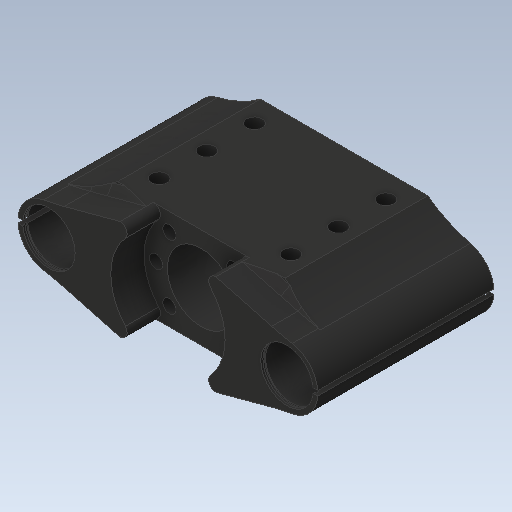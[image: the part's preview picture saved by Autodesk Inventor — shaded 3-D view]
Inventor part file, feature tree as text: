
AUTODESK INVENTOR PART (.ipt)
format: ipt  version: 2020 (Build 240168000, 168)  size: 548,352 bytes
history: native  units: mm
features: sketch x24, extrude x17, other x10, mirror x6, chamfer x5, fillet x3, pattern_circular x2, pattern_linear x1
ambient origin geometry x8: Origin, YZ Plane, XZ Plane, XY Plane, X Axis, Y Axis, Z Axis, Center Point
bodies: Body1 (feature_tree)
feature tree (68):
  other  "Bryła1"
  other  "Opisy"
  extrude  "Wyciągnięcie proste1"  Depth=22.0mm
  extrude  "Wyciągnięcie proste2"  Depth=26.0mm
  other  "Płaszczyzna konstrukcyjna1"
  extrude  "Wyciągnięcie proste3"  Depth=74.0mm TaperAngle=0.0deg
  extrude  "Wyciągnięcie proste4"  Depth=2.0mm
  other  "Płaszczyzna konstrukcyjna2"
  extrude  "Wyciągnięcie proste5"  Depth=1.0mm
  other  "Płaszczyzna konstrukcyjna3"
  mirror  "Odbij1"
  extrude  "Wyciągnięcie proste6"  Depth=80.0mm TaperAngle=0.0deg
  other  "Płaszczyzna konstrukcyjna4"
  mirror  "Odbij2"
  extrude  "Wyciągnięcie proste7"  [1 undecoded]
  sketch  "Szkic9"
  extrude  "Wyciągnięcie proste8"  Depth=22.0mm
  extrude  "Wyciągnięcie proste9"  Depth=19.0mm
  fillet  "Zaokrąglenie1"  Radius=6.0mm
  extrude  "Wyciągnięcie proste10"  Depth=2.0mm
  mirror  "Odbij3"
  chamfer  "Faza1"  Distance=6.0mm
  other  "Płaszczyzna konstrukcyjna5"
  chamfer  "Faza2"  [1 undecoded]
  chamfer  "Faza3"  Distance=23.0mm
  chamfer  "Faza4"  Distance=1.1mm
  fillet  "Zaokrąglenie2"  [1 undecoded]
  sketch  "Szkic13"
  extrude  "Wyciągnięcie proste13"  Depth=8.0mm
  extrude  "Wyciągnięcie proste14"  Depth=100.0mm
  pattern_circular  "Szyk kołowy3"  [2 undecoded]
  pattern_circular  "Szyk kołowy4"  Count=10  [1 undecoded]
  mirror  "Odbij5"
  extrude  "Wyciągnięcie proste15"  Depth=8.0mm
  extrude  "Wyciągnięcie proste16"  Depth=74.0mm TaperAngle=0.0deg
  extrude  "Wyciągnięcie proste17"  [1 undecoded]
  mirror  "Odbij6"
  fillet  "Zaokrąglenie3"  Radius=2.0mm
  chamfer  "Faza5"  Distance=74.0mm
  other  "Płaszczyzna konstrukcyjna6"
  sketch  "Szkic21"
  sketch  "Szkic22"
  extrude  "Wyciągnięcie proste18"  Depth=48.0mm
  pattern_linear  "Szyk prostokątny1"  Count1=5  [1 undecoded]
  mirror  "Odbij7"
  sketch  "Szkic24"
  sketch  "Szkic25"
  extrude  "Wyciągnięcie proste19"  Depth=14.0mm TaperAngle=0.0deg
  sketch  "Szkic27"
  other  "Płaszczyzna konstrukcyjna7"
  sketch  "Szkic28"
  sketch  "Szkic1"
  sketch  "Szkic2"
  sketch  "Szkic4"
  sketch  "Szkic5"
  sketch  "Szkic6"
  sketch  "Szkic7"
  sketch  "Szkic8"
  sketch  "Szkic10"
  sketch  "Szkic11"
  sketch  "Szkic12"
  sketch  "Szkic15"
  sketch  "Szkic18"
  sketch  "Szkic19"
  sketch  "Szkic20"
  sketch  "Szkic23"
  sketch  "Szkic26"
  other  "Wymiar liniowy 1"
note: 8 required parameter values undecoded (feature->parameter linkage not recoverable at this tier; creation-order binding heuristic only, values carry confidence <= 0.55)
